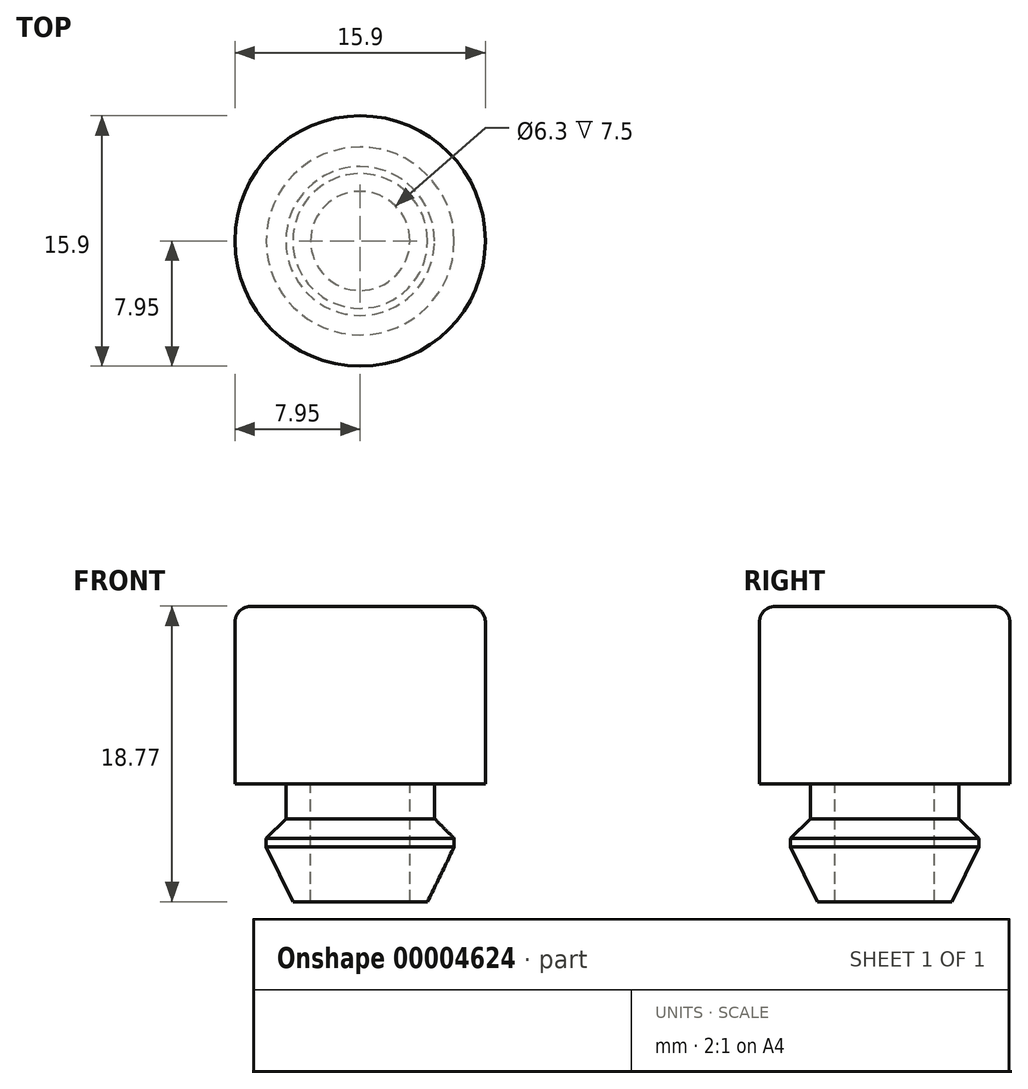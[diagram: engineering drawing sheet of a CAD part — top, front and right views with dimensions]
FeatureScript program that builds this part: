
annotation { "Feature Type Name" : "Feature", "Feature Type Description" : "" }
export const myFeature = defineFeature(function(context is Context, id is Id, definition is map)
    precondition{}
    {
        {
            var Q0;
            Q0=qCreatedBy(makeId("Front.planeOp"),FACE);
            var sketch = newSketch(context, id + "F0", { "sketchPlane" : qUnion([Q0])});
            skLineSegment(sketch, "E0", {"start": v(0, 11.07) * mm, "end": v(0, -10.58) * mm});
            skLineSegment(sketch, "E1", {"start": v(0, 11.07) * mm, "end": v(7.95, 11.07) * mm});
            skLineSegment(sketch, "E2", {"start": v(7.95, 11.07) * mm, "end": v(7.95, -0.2) * mm});
            skLineSegment(sketch, "E3", {"start": v(7.95, -0.2) * mm, "end": v(4.73, -0.2) * mm});
            skLineSegment(sketch, "E4", {"start": v(4.73, -0.2) * mm, "end": v(4.73, -2.43) * mm});
            skLineSegment(sketch, "E5", {"start": v(4.73, -2.43) * mm, "end": v(5.97, -2.43) * mm});
            skLineSegment(sketch, "E6", {"start": v(5.97, -2.43) * mm, "end": v(5.97, -4.21) * mm});
            skLineSegment(sketch, "E7", {"start": v(5.97, -4.21) * mm, "end": v(4.28, -7.7) * mm});
            skLineSegment(sketch, "E8", {"start": v(4.28, -7.7) * mm, "end": v(3.15, -7.7) * mm});
            skLineSegment(sketch, "E9", {"start": v(3.15, -7.7) * mm, "end": v(3.15, -0.2) * mm});
            skLineSegment(sketch, "E10", {"start": v(3.15, -0.2) * mm, "end": v(0, -0.2) * mm});
            skSolve(sketch);
        }
        {
            var Q0;
            {var subQ1=sQuery(id+"F0.wireOp",EDGE,"E1");Q0=makeQuery(id+"F0.imprint","IMPRINT",FACE,{"disambiguationData":[TD([[makeQuery(id+"F0.imprint","IMPRINT",EDGE,{"derivedFrom":subQ1}),-1.0]])]});}
            var Q1;
            Q1=sQuery(id+"F0.wireOp",EDGE,"E0");
            revolve(context, id + "F1", {"entities" : qUnion([Q0]), "axis" : qUnion([Q1]), "revolveType" : RevolveType.FULL});
        }
        {
            var Q0;
            Q0=makeQuery(id+"F1.opRevolve","SWEPT_EDGE",EDGE,{"disambiguationData":[OSD([sQuery(id+"F0.wireOp",EDGE,"E5"),sQuery(id+"F0.wireOp",EDGE,"E6")])]});
            chamfer(context, id + "F2", {"entities" : qUnion([Q0]), "width" : 1.25 * mm, "tangentPropagation" : true});
        }
        {
            var Q0;
            Q0=makeQuery(id+"F1.opRevolve","SWEPT_EDGE",EDGE,{"disambiguationData":[OSD([sQuery(id+"F0.wireOp",EDGE,"E1"),sQuery(id+"F0.wireOp",EDGE,"E2")])]});
            fillet(context, id + "F3", {"entities" : qUnion([Q0]), "radius" : 1 * mm, "tangentPropagation" : true, "allowEdgeOverflow" : false});
        }
    });
